# Revit family: Freestanding_Storage_&_Accessories-Teknion-RACMF_Glass_Markerboard-R2019
name_source: partatom
category: Furniture
units: mm (PartAtom-declared; Revit-internal decimal feet)

## family parameters
Always vertical = Yes
Cut with Voids When Loaded = No
OmniClass Number = 23.40.20.00
OmniClass Title = General Furniture and Specialties
Room Calculation Point = No
Shared = Yes
Work Plane-Based = No

## types (8) — shared parameters
Assembly Code = E2020200
Manufacturer = Teknion
Manufacturer Fax = 416.661.4586
Part Number = RACMF
Product Documentation Link = https://www.teknion.com
Product Line = Expansion Desking
Product Page URL = https://www.teknion.com
Series = Expansion Desking
Sustainability Data = https://www.teknion.com
URL = www.teknion.com
Unit Weight URL = http://www.teknion.com
Warranty = http://www.teknion.com

## per-type parameters (varying)
| type | Bottom of Board Offset | Description | Height | Model |
| Above Floor Starting Height, 42" Finishing Height | 0.72 " | Glass Markerboard – Freestanding Storage Mounted, Above Floor Starting Height, 42" Finishing Height | 41.882 " | RACMF_0142__ |
| Above Worksurface Starting Height, 42" Finishing Height | 30.118 " | Glass Markerboard – Freestanding Storage Mounted, Above Worksurface Starting Height, 42" Finishing Height | 41.882 " | RACMF_3042__ |
| Above Worksurface Starting Height, 51" Finishing Height | 30.118 " | Glass Markerboard – Freestanding Storage Mounted, Above Worksurface Starting Height, 51" Finishing Height | 50.172 " | RACMF_3051__ |
| Above Worksurface Starting Height, 66" Finishing Height | 30.118 " | Glass Markerboard – Freestanding Storage Mounted, Above Worksurface Starting Height, 66" Finishing Height | 66 " | RACMF_3066__ |
| Above Worksurface Starting Height, 72" Finishing Height | 30.118 " | Glass Markerboard – Freestanding Storage Mounted, Above Worksurface Starting Height, 72" Finishing Height | 72 " | RACMF_3072__ |
| Above Floor Starting Height, 51" Finishing Height | 0.72 " | Glass Markerboard – Freestanding Storage Mounted, Above Floor Starting Height, 51" Finishing Height | 50.172 " | RACMF_0151__ |
| Above Floor Starting Height, 66" Finishing Height | 0.72 " | Glass Markerboard – Freestanding Storage Mounted, Above Floor Starting Height, 66" Finishing Height | 66 " | RACMF_0166__ |
| Above Floor Starting Height, 72" Finishing Height | 0.72 " | Glass Markerboard – Freestanding Storage Mounted, Above Floor Starting Height, 72" Finishing Height | 72 " | RACMF_0172__ |

## geometry (parser evidence)
native form markers: Sweep x2
no freeform markers — native parametric forms only
